# Revit family: Toilet_Paper_Holder-American_Standard-Delancey-7052230_Series
name_source: partatom
category: Specialty Equipment
revit_build: Autodesk Revit 2018 (Build: 20170223_1515(x64)
units: mm (PartAtom-declared; Revit-internal decimal feet)

## family parameters
Cut with Voids When Loaded = No
Host = Face
OmniClass Number = 23.40.20.21
OmniClass Title = Toilet and Bath Specialties
Part Type = Normal
Room Calculation Point = No
Round Connector Dimension = Use Diameter
Shared = Yes

## types (4) — shared parameters
Assembly Code = C1030200
Default Elevation = 44"
Description = Delancey® Toilet Paper Holder
Height = 2 3/16"
Installation Type = Wall Mounted
Length = 9 5/16"
Manufacturer = American Standard
Product Documentation Link = https://americanstandard.box.com
Product Page URL = https://www.americanstandard-us.com
URL = https://www.americanstandard-us.com
Warranty Information = Limited Lifetime Warranty on Function and Finish
Width = 3 7/8"

## per-type parameters (varying)
| type | Finish | Material |
| 7052230.002 | Metal-American Standard-002-Polished Chrome | Metal-American Standard-002-Polished Chrome |
| 7052230.295 | Metal-American Standard-295-Brushed Nickel | Metal-American Standard-295-Brushed Nickel |
| 7052230.013 | Metal-American Standard-013-Polished Nickel | Metal-American Standard-013-Polished Nickel |
| 7052230.278 | Metal-American Standard-278-Legacy Bronze | Metal-American Standard-278-Legacy Bronze |

note: column(s) folded — value = type name in every type: Model

## geometry (parser evidence)
native form markers: Sweep x2
no freeform markers — native parametric forms only
